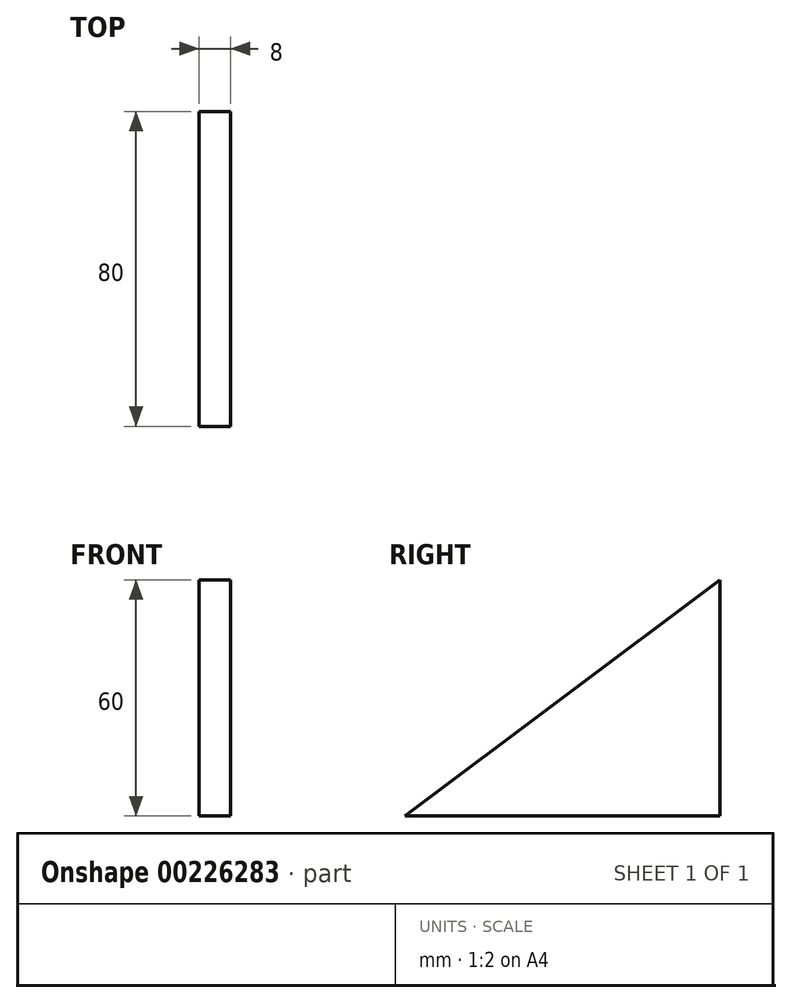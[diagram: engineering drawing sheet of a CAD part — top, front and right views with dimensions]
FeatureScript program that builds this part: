
annotation { "Feature Type Name" : "Feature", "Feature Type Description" : "" }
export const myFeature = defineFeature(function(context is Context, id is Id, definition is map)
    precondition{}
    {
        {
            var Q0;
            Q0=qCreatedBy(makeId("Right.planeOp"),FACE);
            var sketch = newSketch(context, id + "F0", { "sketchPlane" : qUnion([Q0])});
            skLineSegment(sketch, "E0.bottom", {"start": v(2.13, 0) * mm, "end": v(-77.87, 0) * mm});
            skLineSegment(sketch, "E0.left", {"start": v(2.13, 0) * mm, "end": v(2.13, 60) * mm});
            skPoint(sketch, "E0.middle", {"position": v(-37.87, 30) * mm});
            skLineSegment(sketch, "E1", {"start": v(2.13, 60) * mm, "end": v(-77.87, 0) * mm});
            skPoint(sketch, "E0.right.end.orphan", {"position": v(-77.87, 60) * mm});
            skSolve(sketch);
        }
        {
            var Q0;
            Q0 = qSketchRegion(id + "F0", true);
            var Q1;
            Q1=makeQuery(id+"F0.imprint","IMPRINT",FACE,{"disambiguationData":[TD([[makeQuery(id+"F0.imprint","IMPRINT",EDGE,{"derivedFrom":sQuery(id+"F0.wireOp",EDGE,"E0.bottom")}),-1.0]])]});
            extrude(context, id + "F1", {"entities" : qUnion([Q0, Q1]), "depth" : 8 * mm});
        }
    });
